# Revit family: Konsole 45- 90 D Platte längs
name_source: partatom
category: HLS-Bauteile
revit_build: Autodesk Revit 2017 (Build: 20190507_1515(x64)
units: mm (PartAtom-declared; Revit-internal decimal feet)

## family parameters
Basisbauteil = Fläche
Beim Laden mit Abzugskörper schneiden = Nein
Bemaßung runder Anschluss = Durchmesser verwenden
Gemeinsam genutzt = Ja
Raumberechnungspunkt = Nein
Teiletyp = Normal

## types (7) — shared parameters
Ausrichtung Platte = längs
Breite Platte = 55 mm  [stored 0.180446 ft]
Breite Profil = 45 mm  [stored 0.147638 ft]
Fabrikat = MEFA
Firma = MEFA Befestigungs- und Montagesysteme GmbH
Höhe Profil = 90 mm  [stored 0.295276 ft]
Kurztext1 = Konsole C-Profil 45/90
Langloch Platte = 14x20 mm
Lochabstand = 118 mm
Lochdurchmesser = 14 mm
Länge Platte = 160 mm  [stored 0.524934 ft]
Material = Stahl
Materialname C-Profil = S235JR
Materialname Platte = S235JR
Profil = Doppel-C-Profil
Stärke Platte = 12 mm  [stored 0.0393701 ft]
Stärke Profil = 2 mm  [stored 0.00656168 ft]
Vorgabe-Ansicht = 1219 mm

## per-type parameters (varying)
| type | Artikelnummer | EAN | Gewicht | Gewicht pro Bauteil | Kurztext2 | Länge Konsole | Oberflaeche | Schienenlänge | max. zul. Last F1 | max. zul. Last F2 | max. zul. Last q0 |
| Konsole 45- 90 D L=1050 Platte längs gvz | 180901050 | 4250928448408 | 5.97 kg | 5.97 kg | L= 1.050 mm Platte längs gvz | 1 mm  [stored 0.00328084 ft] | galvanisch verzinkt | Montageschiene 45- 90-2,0 D für Konsole : C-Profil 45- 90-2,0 D L= 1050 | 2.98 kN | 1.49 kN | 2.840 kN/m |
| Konsole 45- 90 D L= 945 Platte längs gvz | 180900945 | 4250928448392 | 5.45 kg | 5.45 kg | L= 945 mm Platte längs gvz | 945 mm  [stored 3.10039 ft] | galvanisch verzinkt | Montageschiene 45- 90-2,0 D für Konsole : C-Profil 45- 90-2,0 D L=  945 | 3.31 kN | 1.66 kN | 3.500 kN/m |
| Konsole 45- 90 D L= 840 Platte längs gvz | 180900840 | 4250928448378 | 4.94 kg | 4.94 kg | L= 840 mm Platte längs gvz | 840 mm  [stored 2.75591 ft] | galvanisch verzinkt | Montageschiene 45- 90-2,0 D für Konsole : C-Profil 45- 90-2,0 D L=  840 | 3.72 kN | 1.86 kN | 4.430 kN/m |
| Konsole 45- 90 D L= 735 Platte längs gvz | 180900735 | 4250928448361 | 4.42 kg | 4.42 kg | L= 735 mm Platte längs gvz | 735 mm  [stored 2.41142 ft] | galvanisch verzinkt | Montageschiene 45- 90-2,0 D für Konsole : C-Profil 45- 90-2,0 D L=  735 | 4.26 kN | 2.13 kN | 5.790 kN/m |
| Konsole 45- 90 D L= 840 Platte längs fvz | 180900840/fvz | 4250928448385 | 5.31 kg | 5.31 kg | L= 840 mm Platte längs fsv | 840 mm  [stored 2.75591 ft] | feuerstückverzinkt | Montageschiene 45- 90-2,0 D für Konsole : C-Profil 45- 90-2,0 D L=  840 | 3.72 kN | 1.86 kN | 4.430 kN/m |
| Konsole 45- 90 D L= 630 Platte längs gvz | 180900630 | 4250928448347 | 3.90 kg | 3.90 kg | L= 630 mm Platte längs gvz | 630 mm  [stored 2.06693 ft] | galvanisch verzinkt | Montageschiene 45- 90-2,0 D für Konsole : C-Profil 45- 90-2,0 D L=  630 | 4.97 kN | 2.48 kN | 7.880 kN/m |
| Konsole 45- 90 D L= 630 Platte längs fvz | 180900630/fvz | 4250928448354 | 4.19 kg | 4.19 kg | L= 630 mm Platte längs fsv | 630 mm  [stored 2.06693 ft] | feuerstückverzinkt | Montageschiene 45- 90-2,0 D für Konsole : C-Profil 45- 90-2,0 D L=  630 | 4.97 kN | 2.48 kN | 7.880 kN/m |

note: [stored X ft] marks values corroborated as IEEE doubles in the binary element streams (Revit-internal decimal feet)
